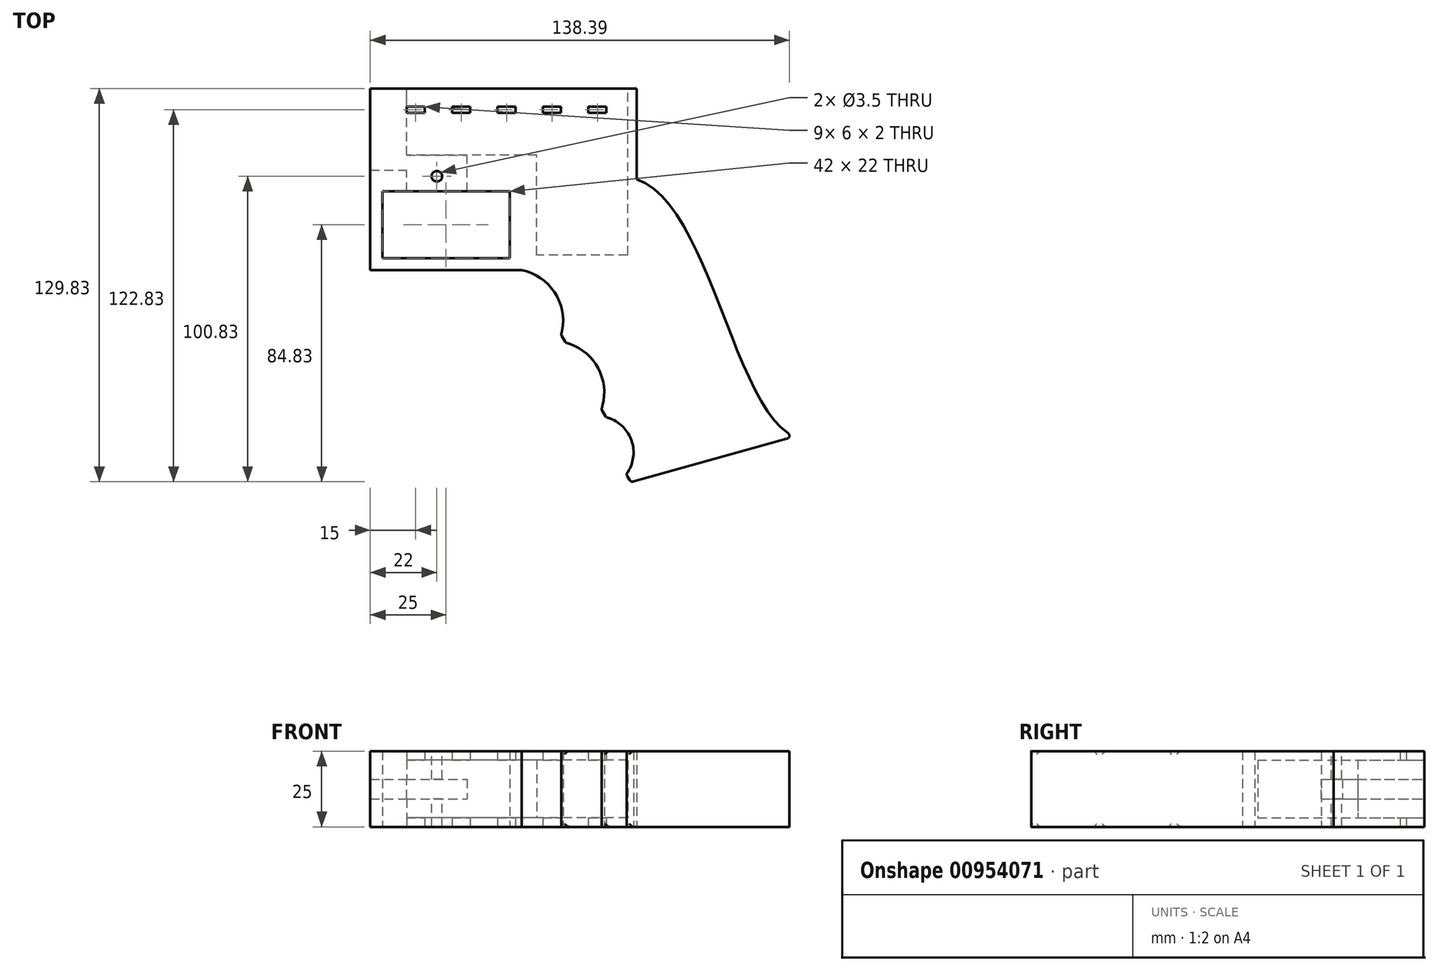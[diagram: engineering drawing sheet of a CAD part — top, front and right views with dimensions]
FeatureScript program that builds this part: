
annotation { "Feature Type Name" : "Feature", "Feature Type Description" : "" }
export const myFeature = defineFeature(function(context is Context, id is Id, definition is map)
    precondition{}
    {
        {
            var Q0;
            Q0=qCreatedBy(makeId("Top.planeOp"),FACE);
            var sketch = newSketch(context, id + "F0", { "sketchPlane" : qUnion([Q0])});
            skLineSegment(sketch, "E0.bottom", {"start": v(-44, 30) * mm, "end": v(44, 30) * mm});
            skLineSegment(sketch, "E0.top", {"start": v(-44, -30) * mm, "end": v(44, -30) * mm});
            skLineSegment(sketch, "E0.left", {"start": v(-44, 30) * mm, "end": v(-44, -30) * mm});
            skLineSegment(sketch, "E0.right", {"start": v(44, 30) * mm, "end": v(44, -30) * mm});
            skPoint(sketch, "E0.middle", {"position": v(0, 0) * mm});
            skLineSegment(sketch, "E1.bottom", {"start": v(-40, -4) * mm, "end": v(2, -4) * mm});
            skLineSegment(sketch, "E1.top", {"start": v(-40, -26) * mm, "end": v(2, -26) * mm});
            skLineSegment(sketch, "E1.left", {"start": v(-40, -4) * mm, "end": v(-40, -26) * mm});
            skLineSegment(sketch, "E1.right", {"start": v(2, -4) * mm, "end": v(2, -26) * mm});
            skLineSegment(sketch, "E2.bottom", {"start": v(-26, 24) * mm, "end": v(-32, 24) * mm});
            skLineSegment(sketch, "E2.top", {"start": v(-26, 22) * mm, "end": v(-32, 22) * mm});
            skLineSegment(sketch, "E2.left", {"start": v(-26, 24) * mm, "end": v(-26, 22) * mm});
            skLineSegment(sketch, "E2.right", {"start": v(-32, 24) * mm, "end": v(-32, 22) * mm});
            skLineSegment(sketch, "E3.1.0.0", {"start": v(-11, 24) * mm, "end": v(-17, 24) * mm});
            skLineSegment(sketch, "E3.1.0.1", {"start": v(-11, 22) * mm, "end": v(-17, 22) * mm});
            skLineSegment(sketch, "E3.1.0.2", {"start": v(-17, 24) * mm, "end": v(-17, 22) * mm});
            skLineSegment(sketch, "E3.1.0.3", {"start": v(-11, 24) * mm, "end": v(-11, 22) * mm});
            skLineSegment(sketch, "E3.2.0.0", {"start": v(4, 24) * mm, "end": v(-2, 24) * mm});
            skLineSegment(sketch, "E3.2.0.1", {"start": v(4, 22) * mm, "end": v(-2, 22) * mm});
            skLineSegment(sketch, "E3.2.0.2", {"start": v(-2, 24) * mm, "end": v(-2, 22) * mm});
            skLineSegment(sketch, "E3.2.0.3", {"start": v(4, 24) * mm, "end": v(4, 22) * mm});
            skLineSegment(sketch, "E3.direction1", {"start": v(-32, 24) * mm, "end": v(-17, 24) * mm, "construction": true});
            skLineSegment(sketch, "E4.0.3.0", {"start": v(19, 24) * mm, "end": v(13, 24) * mm});
            skLineSegment(sketch, "E4.3.3.0", {"start": v(19, 22) * mm, "end": v(13, 22) * mm});
            skLineSegment(sketch, "E4.6.3.0", {"start": v(13, 24) * mm, "end": v(13, 22) * mm});
            skLineSegment(sketch, "E4.9.3.0", {"start": v(19, 24) * mm, "end": v(19, 22) * mm});
            skLineSegment(sketch, "E4.0.4.0", {"start": v(34, 24) * mm, "end": v(28, 24) * mm});
            skLineSegment(sketch, "E4.3.4.0", {"start": v(34, 22) * mm, "end": v(28, 22) * mm});
            skLineSegment(sketch, "E4.6.4.0", {"start": v(28, 24) * mm, "end": v(28, 22) * mm});
            skLineSegment(sketch, "E4.9.4.0", {"start": v(34, 24) * mm, "end": v(34, 22) * mm});
            skFitSpline(sketch, "E5", {"points": [v(44, 0) * mm, v(96, -85) * mm], "startDerivative": vector(71.52, -23) * mm, "endDerivative": vector(59.6, -26.37) * mm});
            skLineSegment(sketch, "E6", {"start": v(96, -85) * mm, "end": v(42.05, -100) * mm});
            skArc(sketch, "E7", {"start": v(19, -51.35) * mm, "mid": v(17.18, -37.83) * mm, "end": v(6, -30) * mm});
            skLineSegment(sketch, "E8", {"start": v(19, -51.35) * mm, "end": v(20.53, -53.94) * mm});
            skArc(sketch, "E9", {"start": v(32.32, -75.98) * mm, "mid": v(31.25, -62.37) * mm, "end": v(20.53, -53.94) * mm});
            skLineSegment(sketch, "E10", {"start": v(32.32, -75.98) * mm, "end": v(33.84, -78.56) * mm});
            skArc(sketch, "E11", {"start": v(40.52, -97.42) * mm, "mid": v(42.24, -86.2) * mm, "end": v(33.84, -78.56) * mm});
            skLineSegment(sketch, "E12", {"start": v(40.52, -97.42) * mm, "end": v(42.05, -100) * mm});
            skSolve(sketch);
        }
        {
            var Q0;
            {var subQ5=sQuery(id+"F0.wireOp",EDGE,"E0.bottom");Q0=makeQuery(id+"F0.imprint","IMPRINT",FACE,{"disambiguationData":[TD([[makeQuery(id+"F0.imprint","IMPRINT",EDGE,{"derivedFrom":subQ5}),-1.0]])]});}
            var Q1;
            {var subQ0=sQuery(id+"F0.wireOp",EDGE,"E5");Q1=makeQuery(id+"F0.imprint","IMPRINT",FACE,{"disambiguationData":[TD([[makeQuery(id+"F0.imprint","IMPRINT",EDGE,{"derivedFrom":subQ0}),-1.0]])]});}
            extrude(context, id + "F1", {"entities" : qUnion([Q0, Q1]), "depth" : 25 * mm, "offsetDistance" : 25 * mm});
        }
        {
            var Q0;
            Q0=makeQuery(id+"F1.opExtrude","SWEPT_FACE",FACE,{"disambiguationData":[OSD([sQuery(id+"F0.wireOp",EDGE,"E0.bottom")])]});
            var sketch = newSketch(context, id + "F2", { "sketchPlane" : qUnion([Q0])});
            skLineSegment(sketch, "E13.bottom", {"start": v(-41, 22) * mm, "end": v(32, 22) * mm});
            skLineSegment(sketch, "E13.top", {"start": v(-41, 3) * mm, "end": v(32, 3) * mm});
            skLineSegment(sketch, "E13.left", {"start": v(-41, 22) * mm, "end": v(-41, 3) * mm});
            skLineSegment(sketch, "E13.right", {"start": v(32, 22) * mm, "end": v(32, 3) * mm});
            skLineSegment(sketch, "E14", {"start": v(-11, 22) * mm, "end": v(-11, 3) * mm});
            skLineSegment(sketch, "E15.bottom", {"start": v(44, 15.75) * mm, "end": v(12, 15.75) * mm});
            skLineSegment(sketch, "E15.top", {"start": v(44, 9.25) * mm, "end": v(12, 9.25) * mm});
            skLineSegment(sketch, "E15.left", {"start": v(44, 15.75) * mm, "end": v(44, 9.25) * mm});
            skLineSegment(sketch, "E15.right", {"start": v(12, 15.75) * mm, "end": v(12, 9.25) * mm});
            skLineSegment(sketch, "E16", {"start": v(24.87, 22) * mm, "end": v(24.87, 15.75) * mm, "construction": true});
            skLineSegment(sketch, "E17", {"start": v(24.87, 3) * mm, "end": v(24.87, 9.25) * mm, "construction": true});
            skPoint(sketch, "E17.startSnap0", {"position": v(24.87, 18.88) * mm});
            skSolve(sketch);
        }
        {
            var Q0;
            {var subQ9=sQuery(id+"F2.wireOp",EDGE,"E14");Q0=makeQuery(id+"F2.imprint","IMPRINT",FACE,{"disambiguationData":[TD([[makeQuery(id+"F2.imprint","IMPRINT",EDGE,{"derivedFrom":subQ9}),1.0]])]});}
            var Q1;
            {var subQ0=sQuery(id+"F2.wireOp",EDGE,"E13.left");Q1=makeQuery(id+"F2.imprint","IMPRINT",FACE,{"disambiguationData":[TD([[makeQuery(id+"F2.imprint","IMPRINT",EDGE,{"derivedFrom":subQ0}),1.0]])]});}
            var Q2;
            {var subQ5=sQuery(id+"F2.wireOp",EDGE,"E15.right");Q2=makeQuery(id+"F2.imprint","IMPRINT",FACE,{"disambiguationData":[TD([[makeQuery(id+"F2.imprint","IMPRINT",EDGE,{"derivedFrom":subQ5}),1.0]])]});}
            var Q3;
            {var subQ5=sQuery(id+"F2.wireOp",EDGE,"E15.left");Q3=makeQuery(id+"F2.imprint","IMPRINT",FACE,{"disambiguationData":[TD([[makeQuery(id+"F2.imprint","IMPRINT",EDGE,{"derivedFrom":subQ5}),-1.0]])]});}
            extrude(context, id + "F3", {"entities" : qUnion([Q0, Q1, Q2, Q3]), "operationType" : NewBodyOperationType.REMOVE, "oppositeDirection" : true, "depth" : 22 * mm, "offsetDistance" : 25 * mm});
        }
        {
            var Q0;
            {var subQ0=sQuery(id+"F2.wireOp",EDGE,"E13.left");Q0=makeQuery(id+"F2.imprint","IMPRINT",FACE,{"disambiguationData":[TD([[makeQuery(id+"F2.imprint","IMPRINT",EDGE,{"derivedFrom":subQ0}),1.0]])]});}
            extrude(context, id + "F4", {"entities" : qUnion([Q0]), "operationType" : NewBodyOperationType.REMOVE, "oppositeDirection" : true, "depth" : 55 * mm, "offsetDistance" : 25 * mm});
        }
        {
            var Q0;
            {var subQ5=sQuery(id+"F2.wireOp",EDGE,"E15.right");Q0=makeQuery(id+"F2.imprint","IMPRINT",FACE,{"disambiguationData":[TD([[makeQuery(id+"F2.imprint","IMPRINT",EDGE,{"derivedFrom":subQ5}),1.0]])]});}
            var Q1;
            Q1=makeQuery(id+"F1.opExtrude","SWEPT_FACE",FACE,{"disambiguationData":[OSD([sQuery(id+"F0.wireOp",EDGE,"E1.bottom")])]});
            extrude(context, id + "F5", {"entities" : qUnion([Q0]), "operationType" : NewBodyOperationType.REMOVE, "endBound" : BoundingType.UP_TO_SURFACE, "oppositeDirection" : true, "depth" : 25 * mm, "endBoundEntityFace" : qUnion([Q1]), "offsetDistance" : 25 * mm});
        }
        {
            var Q0;
            {var subQ5=sQuery(id+"F2.wireOp",EDGE,"E15.left");Q0=makeQuery(id+"F2.imprint","IMPRINT",FACE,{"disambiguationData":[TD([[makeQuery(id+"F2.imprint","IMPRINT",EDGE,{"derivedFrom":subQ5}),-1.0]])]});}
            extrude(context, id + "F6", {"entities" : qUnion([Q0]), "operationType" : NewBodyOperationType.REMOVE, "oppositeDirection" : true, "depth" : 27 * mm, "offsetDistance" : 25 * mm});
        }
        {
            var Q0;
            Q0=makeQuery(id+"F1.opExtrude","SWEPT_FACE",FACE,{"disambiguationData":[OSD([sQuery(id+"F0.wireOp",EDGE,"E8")])]});
            var Q1;
            Q1=makeQuery(id+"F1.opExtrude","SWEPT_FACE",FACE,{"disambiguationData":[OSD([sQuery(id+"F0.wireOp",EDGE,"E10")])]});
            var Q2;
            Q2=makeQuery(id+"F1.opExtrude","SWEPT_FACE",FACE,{"disambiguationData":[OSD([sQuery(id+"F0.wireOp",EDGE,"E12")])]});
            var Q3;
            Q3=makeQuery(id+"F1.opExtrude","SWEPT_EDGE",EDGE,{"disambiguationData":[OSD([sQuery(id+"F0.wireOp",EDGE,"E5"),sQuery(id+"F0.wireOp",EDGE,"E6")])]});
            fillet(context, id + "F7", {"entities" : qUnion([Q0, Q1, Q2, Q3]), "radius" : 1 * mm, "tangentPropagation" : true, "allowEdgeOverflow" : false});
        }
        {
            var Q0;
            Q0=makeQuery(id+"F1.opExtrude","CAP_FACE",FACE,{"disambiguationData":[OSD([sQuery(id+"F0.wireOp",EDGE,"E0.bottom"),sQuery(id+"F0.wireOp",EDGE,"E0.top"),sQuery(id+"F0.wireOp",EDGE,"E0.left"),sQuery(id+"F0.wireOp",EDGE,"E0.right"),sQuery(id+"F0.wireOp",EDGE,"E1.bottom"),sQuery(id+"F0.wireOp",EDGE,"E1.top"),sQuery(id+"F0.wireOp",EDGE,"E1.left"),sQuery(id+"F0.wireOp",EDGE,"E1.right"),sQuery(id+"F0.wireOp",EDGE,"E2.bottom"),sQuery(id+"F0.wireOp",EDGE,"E2.top"),sQuery(id+"F0.wireOp",EDGE,"E2.left"),sQuery(id+"F0.wireOp",EDGE,"E2.right"),sQuery(id+"F0.wireOp",EDGE,"E3.1.0.0"),sQuery(id+"F0.wireOp",EDGE,"E3.1.0.1"),sQuery(id+"F0.wireOp",EDGE,"E3.1.0.2"),sQuery(id+"F0.wireOp",EDGE,"E3.1.0.3"),sQuery(id+"F0.wireOp",EDGE,"E3.2.0.0"),sQuery(id+"F0.wireOp",EDGE,"E3.2.0.1"),sQuery(id+"F0.wireOp",EDGE,"E3.2.0.2"),sQuery(id+"F0.wireOp",EDGE,"E3.2.0.3"),sQuery(id+"F0.wireOp",EDGE,"E4.0.3.0"),sQuery(id+"F0.wireOp",EDGE,"E4.3.3.0"),sQuery(id+"F0.wireOp",EDGE,"E4.6.3.0"),sQuery(id+"F0.wireOp",EDGE,"E4.9.3.0"),sQuery(id+"F0.wireOp",EDGE,"E4.0.4.0"),sQuery(id+"F0.wireOp",EDGE,"E4.3.4.0"),sQuery(id+"F0.wireOp",EDGE,"E4.6.4.0"),sQuery(id+"F0.wireOp",EDGE,"E4.9.4.0"),sQuery(id+"F0.wireOp",EDGE,"E5"),sQuery(id+"F0.wireOp",EDGE,"E6"),sQuery(id+"F0.wireOp",EDGE,"E7"),sQuery(id+"F0.wireOp",EDGE,"E8"),sQuery(id+"F0.wireOp",EDGE,"E9"),sQuery(id+"F0.wireOp",EDGE,"E10"),sQuery(id+"F0.wireOp",EDGE,"E11"),sQuery(id+"F0.wireOp",EDGE,"E12")])],"isStart":false});
            var sketch = newSketch(context, id + "F8", { "sketchPlane" : qUnion([Q0])});
            skCircle(sketch, "E18", {"center": v(-22, 1) * mm, "radius": 1.75 * mm});
            skLineSegment(sketch, "E19.0", {"start": v(-12, -4) * mm, "end": v(-32, -4) * mm});
            skLineSegment(sketch, "E20.0.0", {"start": v(43.04, -99.72) * mm, "end": v(93.66, -85.65) * mm});
            skArc(sketch, "E20.0.1", {"start": v(93.66, -85.65) * mm, "mid": v(94.38, -84.85) * mm, "end": v(93.95, -83.86) * mm});
            skFitSpline(sketch, "E20.0.2", {"points": [v(96, -85) * mm, v(76.13, -76.21) * mm, v(67.84, -7.67) * mm, v(44, 0) * mm]});
            skLineSegment(sketch, "E20.0.3", {"start": v(44, 0) * mm, "end": v(44, 30) * mm});
            skLineSegment(sketch, "E20.0.4", {"start": v(44, 30) * mm, "end": v(-44, 30) * mm});
            skLineSegment(sketch, "E20.0.5", {"start": v(-44, 30) * mm, "end": v(-44, -30) * mm});
            skLineSegment(sketch, "E20.0.6", {"start": v(-44, -30) * mm, "end": v(6, -30) * mm});
            skArc(sketch, "E20.0.7", {"start": v(6, -30) * mm, "mid": v(16.8, -37.22) * mm, "end": v(19.34, -49.96) * mm});
            skLineSegment(sketch, "E20.0.8", {"start": v(19.34, -49.96) * mm, "end": v(21.95, -54.37) * mm});
            skArc(sketch, "E20.0.9", {"start": v(21.95, -54.37) * mm, "mid": v(31.28, -62.43) * mm, "end": v(32.72, -74.68) * mm});
            skLineSegment(sketch, "E20.0.10", {"start": v(32.72, -74.68) * mm, "end": v(35.27, -79.02) * mm});
            skArc(sketch, "E20.0.11", {"start": v(35.27, -79.02) * mm, "mid": v(42.3, -86.38) * mm, "end": v(41.14, -96.5) * mm});
            skLineSegment(sketch, "E20.0.12", {"start": v(41.14, -96.5) * mm, "end": v(43.04, -99.72) * mm});
            skLineSegment(sketch, "E21", {"start": v(-22, 1) * mm, "end": v(-22, -4) * mm, "construction": true});
            skSolve(sketch);
        }
        {
            var Q0;
            Q0=makeQuery(id+"F8.imprint","IMPRINT",FACE,{"disambiguationData":[TD([[makeQuery(id+"F8.imprint","IMPRINT",EDGE,{"derivedFrom":sQuery(id+"F8.wireOp",EDGE,"E18")}),1.0]])]});
            extrude(context, id + "F9", {"entities" : qUnion([Q0]), "operationType" : NewBodyOperationType.REMOVE, "endBound" : BoundingType.THROUGH_ALL, "oppositeDirection" : true, "depth" : 25 * mm, "offsetDistance" : 25 * mm});
        }
    });
